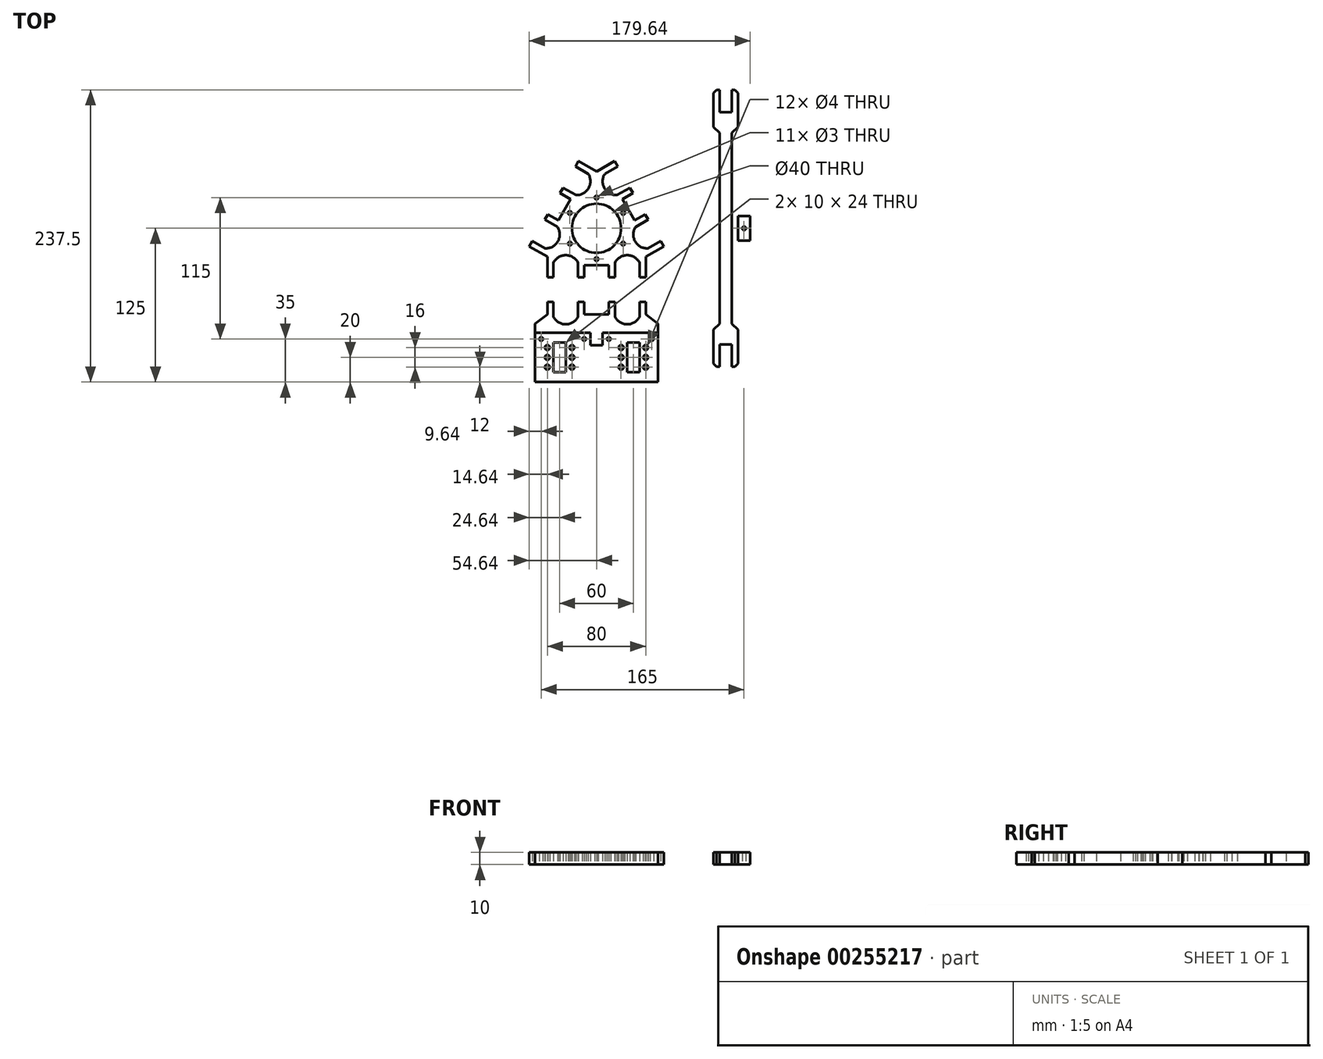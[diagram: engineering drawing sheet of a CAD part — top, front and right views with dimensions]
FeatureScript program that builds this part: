
annotation { "Feature Type Name" : "Feature", "Feature Type Description" : "" }
export const myFeature = defineFeature(function(context is Context, id is Id, definition is map)
    precondition{}
    {
        {
            var Q0;
            Q0=qCreatedBy(makeId("Top.planeOp"),FACE);
            var sketch = newSketch(context, id + "F0", { "sketchPlane" : qUnion([Q0])});
            skCircle(sketch, "E0", {"center": v(0, 0) * mm, "radius": 20 * mm});
            skLineSegment(sketch, "E1", {"start": v(0, 0) * mm, "end": v(-64.79, -37.4) * mm, "construction": true});
            skLineSegment(sketch, "E2", {"start": v(0, 0) * mm, "end": v(0, -241.23) * mm, "construction": true});
            skLineSegment(sketch, "E3", {"start": v(0, 0) * mm, "end": v(62.75, -36.23) * mm, "construction": true});
            skLineSegment(sketch, "E4", {"start": v(0, -30) * mm, "end": v(-10, -30) * mm});
            skLineSegment(sketch, "E5", {"start": v(-10, -30) * mm, "end": v(-10, -40) * mm});
            skLineSegment(sketch, "E6", {"start": v(-10, -40) * mm, "end": v(-15, -40) * mm});
            skLineSegment(sketch, "E7", {"start": v(-15, -40) * mm, "end": v(-15, -28) * mm});
            skLineSegment(sketch, "E8", {"start": v(-15, -28) * mm, "end": v(-35, -28) * mm, "construction": true});
            skLineSegment(sketch, "E9", {"start": v(-35, -28) * mm, "end": v(-35, -40) * mm});
            skLineSegment(sketch, "E10", {"start": v(-35, -40) * mm, "end": v(-40, -40) * mm});
            skLineSegment(sketch, "E11", {"start": v(-40, -40) * mm, "end": v(-40, -23.1) * mm});
            skArc(sketch, "E12", {"start": v(-15, -28) * mm, "mid": v(-25, -21.9) * mm, "end": v(-35, -28) * mm});
            skLineSegment(sketch, "E13.MirrorCS", {"start": v(0, -30) * mm, "end": v(10, -30) * mm});
            skLineSegment(sketch, "E14.MirrorCS", {"start": v(10, -30) * mm, "end": v(10, -40) * mm});
            skLineSegment(sketch, "E15.MirrorCS", {"start": v(10, -40) * mm, "end": v(15, -40) * mm});
            skLineSegment(sketch, "E16.MirrorCS", {"start": v(15, -40) * mm, "end": v(15, -28) * mm});
            skArc(sketch, "E17.MirrorCS", {"start": v(15, -28) * mm, "mid": v(25, -21.9) * mm, "end": v(35, -28) * mm});
            skLineSegment(sketch, "E18.MirrorCS", {"start": v(35, -28) * mm, "end": v(35, -40) * mm});
            skLineSegment(sketch, "E19.MirrorCS", {"start": v(35, -40) * mm, "end": v(40, -40) * mm});
            skLineSegment(sketch, "E20.MirrorCS", {"start": v(40, -40) * mm, "end": v(40, -23.1) * mm});
            skLineSegment(sketch, "E21.1.0", {"start": v(54.64, -14.64) * mm, "end": v(40, -23.1) * mm});
            skLineSegment(sketch, "E21.1.1", {"start": v(52.14, -10.31) * mm, "end": v(54.64, -14.64) * mm});
            skLineSegment(sketch, "E21.1.2", {"start": v(41.75, -16.31) * mm, "end": v(52.14, -10.31) * mm});
            skArc(sketch, "E21.1.3", {"start": v(31.75, 1) * mm, "mid": v(31.47, -10.7) * mm, "end": v(41.75, -16.31) * mm});
            skLineSegment(sketch, "E21.1.4", {"start": v(42.14, 7) * mm, "end": v(31.75, 1) * mm});
            skLineSegment(sketch, "E21.1.5", {"start": v(39.64, 11.34) * mm, "end": v(42.14, 7) * mm});
            skLineSegment(sketch, "E21.1.6", {"start": v(30.98, 6.34) * mm, "end": v(39.64, 11.34) * mm});
            skLineSegment(sketch, "E21.1.7", {"start": v(25.98, 15) * mm, "end": v(30.98, 6.34) * mm});
            skLineSegment(sketch, "E21.1.8", {"start": v(25.98, 15) * mm, "end": v(20.98, 23.66) * mm});
            skLineSegment(sketch, "E21.1.9", {"start": v(20.98, 23.66) * mm, "end": v(29.64, 28.66) * mm});
            skLineSegment(sketch, "E21.1.10", {"start": v(29.64, 28.66) * mm, "end": v(27.14, 33) * mm});
            skLineSegment(sketch, "E21.1.11", {"start": v(27.14, 33) * mm, "end": v(16.75, 27) * mm});
            skArc(sketch, "E21.1.12", {"start": v(16.75, 27) * mm, "mid": v(6.47, 32.6) * mm, "end": v(6.75, 44.31) * mm});
            skLineSegment(sketch, "E21.1.13", {"start": v(6.75, 44.31) * mm, "end": v(17.14, 50.31) * mm});
            skLineSegment(sketch, "E21.1.14", {"start": v(17.14, 50.31) * mm, "end": v(14.64, 54.64) * mm});
            skLineSegment(sketch, "E21.1.15", {"start": v(14.64, 54.64) * mm, "end": v(0, 46.19) * mm});
            skLineSegment(sketch, "E21.2.0", {"start": v(-14.64, 54.64) * mm, "end": v(0, 46.19) * mm});
            skLineSegment(sketch, "E21.2.1", {"start": v(-17.14, 50.31) * mm, "end": v(-14.64, 54.64) * mm});
            skLineSegment(sketch, "E21.2.2", {"start": v(-6.75, 44.31) * mm, "end": v(-17.14, 50.31) * mm});
            skArc(sketch, "E21.2.3", {"start": v(-16.75, 27) * mm, "mid": v(-6.47, 32.6) * mm, "end": v(-6.75, 44.31) * mm});
            skLineSegment(sketch, "E21.2.4", {"start": v(-27.14, 33) * mm, "end": v(-16.75, 27) * mm});
            skLineSegment(sketch, "E21.2.5", {"start": v(-29.64, 28.66) * mm, "end": v(-27.14, 33) * mm});
            skLineSegment(sketch, "E21.2.6", {"start": v(-20.98, 23.66) * mm, "end": v(-29.64, 28.66) * mm});
            skLineSegment(sketch, "E21.2.7", {"start": v(-25.98, 15) * mm, "end": v(-20.98, 23.66) * mm});
            skLineSegment(sketch, "E21.2.8", {"start": v(-25.98, 15) * mm, "end": v(-30.98, 6.34) * mm});
            skLineSegment(sketch, "E21.2.9", {"start": v(-30.98, 6.34) * mm, "end": v(-39.64, 11.34) * mm});
            skLineSegment(sketch, "E21.2.10", {"start": v(-39.64, 11.34) * mm, "end": v(-42.14, 7) * mm});
            skLineSegment(sketch, "E21.2.11", {"start": v(-42.14, 7) * mm, "end": v(-31.75, 1) * mm});
            skArc(sketch, "E21.2.12", {"start": v(-31.75, 1) * mm, "mid": v(-31.47, -10.7) * mm, "end": v(-41.75, -16.31) * mm});
            skLineSegment(sketch, "E21.2.13", {"start": v(-41.75, -16.31) * mm, "end": v(-52.14, -10.31) * mm});
            skLineSegment(sketch, "E21.2.14", {"start": v(-52.14, -10.31) * mm, "end": v(-54.64, -14.64) * mm});
            skLineSegment(sketch, "E21.2.15", {"start": v(-54.64, -14.64) * mm, "end": v(-40, -23.1) * mm});
            skCircle(sketch, "E22", {"center": v(0, 0) * mm, "radius": 25 * mm, "construction": true});
            skCircle(sketch, "E23", {"center": v(0, -25) * mm, "radius": 1.5 * mm});
            skCircle(sketch, "E24.1.0", {"center": v(21.65, -12.5) * mm, "radius": 1.5 * mm});
            skCircle(sketch, "E24.2.0", {"center": v(21.65, 12.5) * mm, "radius": 1.5 * mm});
            skCircle(sketch, "E24.3.0", {"center": v(0, 25) * mm, "radius": 1.5 * mm});
            skCircle(sketch, "E24.4.0", {"center": v(-21.65, 12.5) * mm, "radius": 1.5 * mm});
            skCircle(sketch, "E24.5.0", {"center": v(-21.65, -12.5) * mm, "radius": 1.5 * mm});
            skLineSegment(sketch, "E25", {"start": v(0, -50) * mm, "end": v(56.4, -50) * mm, "construction": true});
            skLineSegment(sketch, "E26.MirrorCS", {"start": v(-40, -60) * mm, "end": v(-40, -76.9) * mm});
            skLineSegment(sketch, "E27.MirrorCS", {"start": v(-35, -60) * mm, "end": v(-40, -60) * mm});
            skLineSegment(sketch, "E28.MirrorCS", {"start": v(-35, -72) * mm, "end": v(-35, -60) * mm});
            skArc(sketch, "E29.MirrorCS", {"start": v(-15, -72) * mm, "mid": v(-25, -78.1) * mm, "end": v(-35, -72) * mm});
            skLineSegment(sketch, "E30.MirrorCS", {"start": v(-15, -60) * mm, "end": v(-15, -72) * mm});
            skLineSegment(sketch, "E31.MirrorCS", {"start": v(-10, -60) * mm, "end": v(-15, -60) * mm});
            skLineSegment(sketch, "E32.MirrorCS", {"start": v(-10, -70) * mm, "end": v(-10, -60) * mm});
            skLineSegment(sketch, "E33.MirrorCS", {"start": v(0, -70) * mm, "end": v(-10, -70) * mm});
            skLineSegment(sketch, "E34.MirrorCS", {"start": v(0, -70) * mm, "end": v(10, -70) * mm});
            skLineSegment(sketch, "E35.MirrorCS", {"start": v(10, -70) * mm, "end": v(10, -60) * mm});
            skLineSegment(sketch, "E36.MirrorCS", {"start": v(10, -60) * mm, "end": v(15, -60) * mm});
            skLineSegment(sketch, "E37.MirrorCS", {"start": v(15, -60) * mm, "end": v(15, -72) * mm});
            skArc(sketch, "E38.MirrorCS", {"start": v(15, -72) * mm, "mid": v(25, -78.1) * mm, "end": v(35, -72) * mm});
            skLineSegment(sketch, "E39.MirrorCS", {"start": v(35, -72) * mm, "end": v(35, -60) * mm});
            skLineSegment(sketch, "E40.MirrorCS", {"start": v(35, -60) * mm, "end": v(40, -60) * mm});
            skLineSegment(sketch, "E41.MirrorCS", {"start": v(40, -60) * mm, "end": v(40, -76.9) * mm});
            skLineSegment(sketch, "E42", {"start": v(0, -95) * mm, "end": v(-5, -95) * mm});
            skLineSegment(sketch, "E43", {"start": v(-5, -95) * mm, "end": v(-5, -85) * mm});
            skLineSegment(sketch, "E44", {"start": v(-5, -85) * mm, "end": v(-50, -85) * mm});
            skLineSegment(sketch, "E45", {"start": v(-50, -85) * mm, "end": v(-50, -77.5) * mm});
            skLineSegment(sketch, "E46", {"start": v(-50, -77.5) * mm, "end": v(-40, -70) * mm});
            skLineSegment(sketch, "E47.MirrorCS", {"start": v(0, -95) * mm, "end": v(5, -95) * mm});
            skLineSegment(sketch, "E48.MirrorCS", {"start": v(5, -95) * mm, "end": v(5, -85) * mm});
            skLineSegment(sketch, "E49.MirrorCS", {"start": v(5, -85) * mm, "end": v(50, -85) * mm});
            skLineSegment(sketch, "E50.MirrorCS", {"start": v(50, -85) * mm, "end": v(50, -77.5) * mm});
            skLineSegment(sketch, "E51.MirrorCS", {"start": v(50, -77.5) * mm, "end": v(40, -70) * mm});
            skLineSegment(sketch, "E52", {"start": v(-50, -85) * mm, "end": v(-50, -125) * mm});
            skLineSegment(sketch, "E53", {"start": v(-50, -125) * mm, "end": v(50, -125) * mm});
            skLineSegment(sketch, "E54", {"start": v(50, -125) * mm, "end": v(50, -85) * mm});
            skCircle(sketch, "E55", {"center": v(10, -90) * mm, "radius": 1.5 * mm});
            skCircle(sketch, "E56", {"center": v(45, -90) * mm, "radius": 1.5 * mm});
            skLineSegment(sketch, "E57.bottom", {"start": v(35, -93) * mm, "end": v(25, -93) * mm});
            skLineSegment(sketch, "E57.top", {"start": v(35, -117) * mm, "end": v(25, -117) * mm});
            skLineSegment(sketch, "E57.left", {"start": v(35, -93) * mm, "end": v(35, -117) * mm});
            skLineSegment(sketch, "E57.right", {"start": v(25, -93) * mm, "end": v(25, -117) * mm});
            skPoint(sketch, "E57.middle", {"position": v(30, -105) * mm});
            skCircle(sketch, "E58", {"center": v(40, -97) * mm, "radius": 2 * mm});
            skCircle(sketch, "E59", {"center": v(40, -105) * mm, "radius": 2 * mm});
            skCircle(sketch, "E60", {"center": v(40, -113) * mm, "radius": 2 * mm});
            skLineSegment(sketch, "E61", {"start": v(30, -105) * mm, "end": v(30, -93) * mm, "construction": true});
            skCircle(sketch, "E62.MirrorC", {"center": v(20, -97) * mm, "radius": 2 * mm});
            skCircle(sketch, "E63.MirrorC", {"center": v(20, -105) * mm, "radius": 2 * mm});
            skCircle(sketch, "E64.MirrorC", {"center": v(20, -113) * mm, "radius": 2 * mm});
            skCircle(sketch, "E65.MirrorC", {"center": v(-10, -90) * mm, "radius": 1.5 * mm});
            skCircle(sketch, "E66.MirrorC", {"center": v(-45, -90) * mm, "radius": 1.5 * mm});
            skCircle(sketch, "E67.MirrorC", {"center": v(-20, -97) * mm, "radius": 2 * mm});
            skCircle(sketch, "E68.MirrorC", {"center": v(-20, -105) * mm, "radius": 2 * mm});
            skCircle(sketch, "E69.MirrorC", {"center": v(-20, -113) * mm, "radius": 2 * mm});
            skCircle(sketch, "E70.MirrorC", {"center": v(-40, -113) * mm, "radius": 2 * mm});
            skCircle(sketch, "E71.MirrorC", {"center": v(-40, -105) * mm, "radius": 2 * mm});
            skCircle(sketch, "E72.MirrorC", {"center": v(-40, -97) * mm, "radius": 2 * mm});
            skLineSegment(sketch, "E73.MirrorCS", {"start": v(-35, -93) * mm, "end": v(-25, -93) * mm});
            skLineSegment(sketch, "E74.MirrorCS", {"start": v(-35, -93) * mm, "end": v(-35, -117) * mm});
            skLineSegment(sketch, "E75.MirrorCS", {"start": v(-35, -117) * mm, "end": v(-25, -117) * mm});
            skLineSegment(sketch, "E76.MirrorCS", {"start": v(-25, -93) * mm, "end": v(-25, -117) * mm});
            skLineSegment(sketch, "E77", {"start": v(0, 0) * mm, "end": v(160, 0) * mm, "construction": true});
            skLineSegment(sketch, "E78", {"start": v(100, 0) * mm, "end": v(100, 77.5) * mm});
            skLineSegment(sketch, "E79", {"start": v(100, 77.5) * mm, "end": v(95, 82.5) * mm});
            skLineSegment(sketch, "E80", {"start": v(95, 82.5) * mm, "end": v(95, 110) * mm});
            skLineSegment(sketch, "E81", {"start": v(95, 110) * mm, "end": v(97.5, 112.5) * mm});
            skLineSegment(sketch, "E82", {"start": v(97.5, 112.5) * mm, "end": v(100, 112.5) * mm});
            skLineSegment(sketch, "E83", {"start": v(100, 112.5) * mm, "end": v(100, 94.5) * mm});
            skLineSegment(sketch, "E84", {"start": v(100, 94.5) * mm, "end": v(110, 94.5) * mm});
            skLineSegment(sketch, "E85", {"start": v(110, 94.5) * mm, "end": v(110, 112.5) * mm});
            skLineSegment(sketch, "E86", {"start": v(110, 112.5) * mm, "end": v(112.5, 112.5) * mm});
            skLineSegment(sketch, "E87", {"start": v(112.5, 112.5) * mm, "end": v(115, 110) * mm});
            skLineSegment(sketch, "E88", {"start": v(115, 110) * mm, "end": v(115, 82.5) * mm});
            skLineSegment(sketch, "E89", {"start": v(115, 82.5) * mm, "end": v(110, 77.5) * mm});
            skLineSegment(sketch, "E90", {"start": v(110, 77.5) * mm, "end": v(110, 0) * mm});
            skLineSegment(sketch, "E91", {"start": v(100, 0) * mm, "end": v(110, 0) * mm, "construction": true});
            skLineSegment(sketch, "E92.MirrorCS", {"start": v(100, 0) * mm, "end": v(100, -77.5) * mm});
            skLineSegment(sketch, "E93.MirrorCS", {"start": v(100, -77.5) * mm, "end": v(95, -82.5) * mm});
            skLineSegment(sketch, "E94.MirrorCS", {"start": v(95, -82.5) * mm, "end": v(95, -110) * mm});
            skLineSegment(sketch, "E95.MirrorCS", {"start": v(95, -110) * mm, "end": v(97.5, -112.5) * mm});
            skLineSegment(sketch, "E96.MirrorCS", {"start": v(97.5, -112.5) * mm, "end": v(100, -112.5) * mm});
            skLineSegment(sketch, "E97.MirrorCS", {"start": v(100, -112.5) * mm, "end": v(100, -94.5) * mm});
            skLineSegment(sketch, "E98.MirrorCS", {"start": v(100, -94.5) * mm, "end": v(110, -94.5) * mm});
            skLineSegment(sketch, "E99.MirrorCS", {"start": v(110, -94.5) * mm, "end": v(110, -112.5) * mm});
            skLineSegment(sketch, "E100.MirrorCS", {"start": v(110, -112.5) * mm, "end": v(112.5, -112.5) * mm});
            skLineSegment(sketch, "E101.MirrorCS", {"start": v(112.5, -112.5) * mm, "end": v(115, -110) * mm});
            skLineSegment(sketch, "E102.MirrorCS", {"start": v(115, -110) * mm, "end": v(115, -82.5) * mm});
            skLineSegment(sketch, "E103.MirrorCS", {"start": v(115, -82.5) * mm, "end": v(110, -77.5) * mm});
            skLineSegment(sketch, "E104.MirrorCS", {"start": v(110, -77.5) * mm, "end": v(110, 0) * mm});
            skLineSegment(sketch, "E105.bottom", {"start": v(125, 10) * mm, "end": v(115, 10) * mm});
            skLineSegment(sketch, "E105.top", {"start": v(125, -10) * mm, "end": v(115, -10) * mm});
            skLineSegment(sketch, "E105.left", {"start": v(125, 10) * mm, "end": v(125, -10) * mm});
            skLineSegment(sketch, "E105.right", {"start": v(115, 10) * mm, "end": v(115, -10) * mm});
            skPoint(sketch, "E105.middle", {"position": v(120, 0) * mm});
            skCircle(sketch, "E106", {"center": v(120, 0) * mm, "radius": 1.5 * mm});
            skSolve(sketch);
        }
        {
            var Q0;
            Q0=makeQuery(id+"F0.imprint","IMPRINT",FACE,{"disambiguationData":[TD([[makeQuery(id+"F0.imprint","IMPRINT",EDGE,{"derivedFrom":sQuery(id+"F0.wireOp",EDGE,"E0")}),-1.0]])]});
            var Q1;
            Q1=makeQuery(id+"F0.imprint","IMPRINT",FACE,{"disambiguationData":[TD([[makeQuery(id+"F0.imprint","IMPRINT",EDGE,{"derivedFrom":sQuery(id+"F0.wireOp",EDGE,"E42")}),1.0]])]});
            var Q2;
            Q2=makeQuery(id+"F0.imprint","IMPRINT",FACE,{"disambiguationData":[TD([[makeQuery(id+"F0.imprint","IMPRINT",EDGE,{"derivedFrom":sQuery(id+"F0.wireOp",EDGE,"E78")}),-1.0]])]});
            var Q3;
            Q3=makeQuery(id+"F0.imprint","IMPRINT",FACE,{"disambiguationData":[TD([[makeQuery(id+"F0.imprint","IMPRINT",EDGE,{"derivedFrom":sQuery(id+"F0.wireOp",EDGE,"E105.bottom")}),1.0]])]});
            var Q4;
            Q4=makeQuery(id+"F0.imprint","IMPRINT",FACE,{"disambiguationData":[TD([[makeQuery(id+"F0.imprint","IMPRINT",EDGE,{"derivedFrom":sQuery(id+"F0.wireOp",EDGE,"luGP7GjI-qIpz-kXm2-CYNx-y5ok2S3jDu1K.bottom")}),-1.0]])]});
            extrude(context, id + "F1", {"entities" : qUnion([Q0, Q1, Q2, Q3, Q4]), "depth" : 10 * mm});
        }
        {
            var Q0;
            {var subQ4=sQuery(id+"F0.wireOp",EDGE,"E27.MirrorCS");Q0=makeQuery(id+"F0.imprint","IMPRINT",FACE,{"disambiguationData":[TD([[makeQuery(id+"F0.imprint","IMPRINT",EDGE,{"derivedFrom":subQ4}),1.0]])]});}
            var Q1;
            Q1=makeQuery(id+"F0.imprint","IMPRINT",FACE,{"disambiguationData":[TD([[makeQuery(id+"F0.imprint","IMPRINT",EDGE,{"derivedFrom":sQuery(id+"F0.wireOp",EDGE,"luGP7GjI-qIpz-kXm2-CYNx-y5ok2S3jDu1K.right")}),1.0]])]});
            extrude(context, id + "F2", {"entities" : qUnion([Q0, Q1]), "depth" : 10 * mm});
        }
    });
